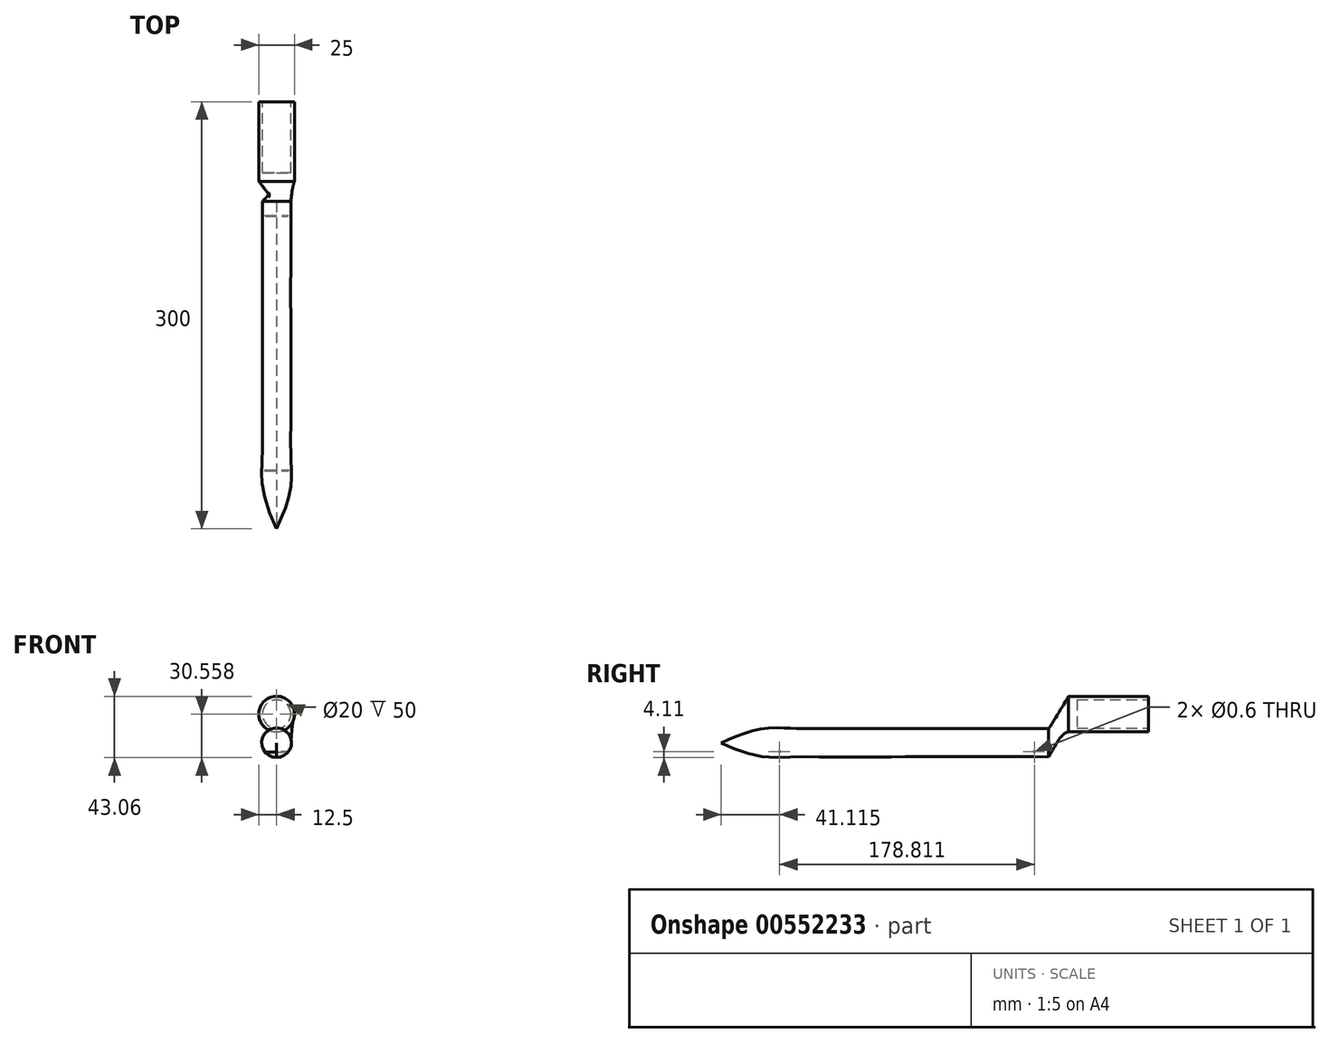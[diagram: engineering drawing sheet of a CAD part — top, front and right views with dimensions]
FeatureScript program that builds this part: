
annotation { "Feature Type Name" : "Feature", "Feature Type Description" : "" }
export const myFeature = defineFeature(function(context is Context, id is Id, definition is map)
    precondition{}
    {
        {
            var Q0;
            Q0=qCreatedBy(makeId("Right.planeOp"),FACE);
            var sketch = newSketch(context, id + "F0", { "sketchPlane" : qUnion([Q0])});
            skLineSegment(sketch, "E0.top", {"start": v(-74.77, -35) * mm, "end": v(75.63, -35) * mm});
            skLineSegment(sketch, "E0.right", {"start": v(150, 15.16) * mm, "end": v(150, -6.84) * mm});
            skPoint(sketch, "E1.orphan", {"position": v(-150, -15) * mm});
            skPoint(sketch, "E2.orphan", {"position": v(-150, -35) * mm});
            skPoint(sketch, "E3.orphan", {"position": v(150, 35) * mm});
            skLineSegment(sketch, "E4", {"start": v(150, 35) * mm, "end": v(80, 23.33) * mm});
            skLineSegment(sketch, "E5", {"start": v(-150, -35) * mm, "end": v(-150, -15) * mm});
            skLineSegment(sketch, "E6", {"start": v(-150, -35) * mm, "end": v(-74.77, -35) * mm});
            skLineSegment(sketch, "E7", {"start": v(150, 35) * mm, "end": v(150, -35) * mm});
            skLineSegment(sketch, "E8", {"start": v(75.63, -35) * mm, "end": v(150, -35) * mm});
            skPoint(sketch, "E9.0.internal.orphan", {"position": v(-150, -25) * mm});
            skLineSegment(sketch, "E10", {"start": v(-150, -15) * mm, "end": v(80, -15) * mm});
            skLineSegment(sketch, "E11", {"start": v(80, -15) * mm, "end": v(80, 23.33) * mm});
            skSolve(sketch);
        }
        {
            var Q0;
            Q0=makeQuery(id+"F0.imprint","IMPRINT",FACE,{"disambiguationData":[TD([[makeQuery(id+"F0.imprint","IMPRINT",EDGE,{"derivedFrom":sQuery(id+"F0.wireOp",EDGE,"E0.bottom")}),-1.0]])]});
            var Q1;
            Q1=makeQuery(id+"F0.imprint","IMPRINT",FACE,{"disambiguationData":[TD([[makeQuery(id+"F0.imprint","IMPRINT",EDGE,{"derivedFrom":sQuery(id+"F0.wireOp",EDGE,"E0.top")}),1.0]])]});
            extrude(context, id + "F1", {"entities" : qUnion([Q0, Q1]), "endBound" : BoundingType.SYMMETRIC, "depth" : 42 * mm, "offsetDistance" : 25 * mm});
        }
        {
            var Q0;
            Q0=makeQuery(id+"F1.opExtrude","SWEPT_FACE",FACE,{"disambiguationData":[OSD([sQuery(id+"F0.wireOp",EDGE,"E7")])]});
            var sketch = newSketch(context, id + "F2", { "sketchPlane" : qUnion([Q0])});
            skPoint(sketch, "E12.start.orphan", {"position": v(0, 35) * mm});
            skCircle(sketch, "E13", {"center": v(0, -4.85) * mm, "radius": 10 * mm});
            skPoint(sketch, "E14.orphan", {"position": v(0, -35) * mm});
            skSolve(sketch);
        }
        {
            var Q0;
            Q0=makeQuery(id+"F2.imprint","IMPRINT",FACE,{"disambiguationData":[TD([[makeQuery(id+"F2.imprint","IMPRINT",EDGE,{"derivedFrom":sQuery(id+"F2.wireOp",EDGE,"E13")}),1.0]])]});
            extrude(context, id + "F3", {"entities" : qUnion([Q0]), "operationType" : NewBodyOperationType.REMOVE, "oppositeDirection" : true, "depth" : 50 * mm, "offsetDistance" : 25 * mm});
        }
        {
            var Q0;
            Q0=makeQuery(id+"F1.opExtrude","SWEPT_FACE",FACE,{"disambiguationData":[OSD([sQuery(id+"F0.wireOp",EDGE,"E5")])]});
            var sketch = newSketch(context, id + "F4", { "sketchPlane" : qUnion([Q0])});
            skLineSegment(sketch, "E15.bottom", {"start": v(-10, -15) * mm, "end": v(10, -15) * mm});
            skLineSegment(sketch, "E15.top", {"start": v(-10, -35) * mm, "end": v(10, -35) * mm});
            skLineSegment(sketch, "E15.left", {"start": v(-10, -15) * mm, "end": v(-10, -35) * mm});
            skLineSegment(sketch, "E15.right", {"start": v(10, -15) * mm, "end": v(10, -35) * mm});
            skPoint(sketch, "E15.middle", {"position": v(0, -25) * mm});
            skPoint(sketch, "E15.middle.positionSnap0", {"position": v(21, -25) * mm});
            skPoint(sketch, "E15.middle.positionSnap1", {"position": v(0, -35) * mm});
            skPoint(sketch, "E15.centerSnap0", {"position": v(21, -25) * mm});
            skPoint(sketch, "E15.centerSnap1", {"position": v(0, -35) * mm});
            skSolve(sketch);
        }
        {
            var Q0;
            Q0=makeQuery(id+"F4.imprint","IMPRINT",FACE,{"disambiguationData":[TD([[makeQuery(id+"F4.imprint","IMPRINT",EDGE,{"derivedFrom":sQuery(id+"F4.wireOp",EDGE,"E15.bottom")}),1.0]])]});
            extrude(context, id + "F5", {"entities" : qUnion([Q0]), "operationType" : NewBodyOperationType.REMOVE, "oppositeDirection" : true, "depth" : 230 * mm, "offsetDistance" : 25 * mm});
        }
        {
            var Q0;
            Q0=qCreatedBy(makeId("Front.planeOp"),FACE);
            cPlane(context, id + "F6", {"entities" : qUnion([Q0]), "cplaneType" : CPlaneType.OFFSET, "offset" : 150 * mm, "width" : 150 * mm, "height" : 150 * mm});
        }
        {
            var Q0;
            Q0=qCreatedBy(id+"F6.planeOp",FACE);
            var sketch = newSketch(context, id + "F7", { "sketchPlane" : qUnion([Q0])});
            skPoint(sketch, "E16", {"position": v(0, -25.1) * mm});
            skSolve(sketch);
        }
        {
            var Q0;
            Q0=qCreatedBy(id+"F6.planeOp",FACE);
            cPlane(context, id + "F8", {"entities" : qUnion([Q0]), "cplaneType" : CPlaneType.OFFSET, "offset" : 30 * mm, "oppositeDirection" : true, "width" : 150 * mm, "height" : 150 * mm});
        }
        {
            var Q0;
            Q0=qCreatedBy(id+"F8.planeOp",FACE);
            var sketch = newSketch(context, id + "F9", { "sketchPlane" : qUnion([Q0])});
            skCircle(sketch, "E17", {"center": v(0, -25.02) * mm, "radius": 10 * mm});
            skSolve(sketch);
        }
        {
            var Q0;
            Q0=qCreatedBy(id+"F6.planeOp",FACE);
            cPlane(context, id + "F10", {"entities" : qUnion([Q0]), "cplaneType" : CPlaneType.OFFSET, "offset" : 230 * mm, "oppositeDirection" : true, "width" : 150 * mm, "height" : 150 * mm});
        }
        {
            var Q0;
            Q0=qCreatedBy(id+"F10.planeOp",FACE);
            var sketch = newSketch(context, id + "F11", { "sketchPlane" : qUnion([Q0])});
            skCircle(sketch, "E18", {"center": v(0, -24.92) * mm, "radius": 10 * mm});
            skSolve(sketch);
        }
        {
            var Q0;
            Q0=qCreatedBy(id+"F6.planeOp",FACE);
            cPlane(context, id + "F12", {"entities" : qUnion([Q0]), "cplaneType" : CPlaneType.OFFSET, "offset" : 115 * mm, "oppositeDirection" : true, "width" : 150 * mm, "height" : 150 * mm});
        }
        {
            var Q0;
            Q0=qCreatedBy(id+"F12.planeOp",FACE);
            var sketch = newSketch(context, id + "F13", { "sketchPlane" : qUnion([Q0])});
            skCircle(sketch, "E19", {"center": v(0, -24.97) * mm, "radius": 10 * mm});
            skSolve(sketch);
        }
        {
            var Q0;
            {var subQ4=sQuery(id+"F0.wireOp",EDGE,"E5");Q0=makeQuery(id+"F5.boolean.opBoolean","SPLIT",FACE,{"disambiguationData":[TD([makeQuery(id+"F5.opExtrude","SWEPT_FACE",FACE,{"disambiguationData":[OSD([sQuery(id+"F4.wireOp",EDGE,"E15.right")])]})])],"derivedFrom":makeQuery(id+"F1.opExtrude","SWEPT_FACE",FACE,{"disambiguationData":[OSD([subQ4])]})});}
            var Q1;
            {var subQ4=sQuery(id+"F0.wireOp",EDGE,"E5");Q1=makeQuery(id+"F5.boolean.opBoolean","SPLIT",FACE,{"disambiguationData":[TD([makeQuery(id+"F5.opExtrude","SWEPT_FACE",FACE,{"disambiguationData":[OSD([sQuery(id+"F4.wireOp",EDGE,"E15.left")])]})])],"derivedFrom":makeQuery(id+"F1.opExtrude","SWEPT_FACE",FACE,{"disambiguationData":[OSD([subQ4])]})});}
            extrude(context, id + "F14", {"entities" : qUnion([Q0, Q1]), "operationType" : NewBodyOperationType.REMOVE, "oppositeDirection" : true, "depth" : 230 * mm, "offsetDistance" : 25 * mm});
        }
        {
            var Q0;
            Q0=qCreatedBy(id+"F8.planeOp",FACE);
            cPlane(context, id + "F15", {"entities" : qUnion([Q0]), "cplaneType" : CPlaneType.OFFSET, "offset" : 45 * mm, "oppositeDirection" : true, "width" : 150 * mm, "height" : 150 * mm});
        }
        {
            var Q0;
            Q0=qCreatedBy(id+"F15.planeOp",FACE);
            var sketch = newSketch(context, id + "F16", { "sketchPlane" : qUnion([Q0])});
            skCircle(sketch, "E20", {"center": v(0, -25.05) * mm, "radius": 10 * mm});
            skSolve(sketch);
        }
        {
            var Q0;
            Q0=qCreatedBy(id+"F15.planeOp",FACE);
            cPlane(context, id + "F17", {"entities" : qUnion([Q0]), "cplaneType" : CPlaneType.OFFSET, "offset" : 23 * mm, "width" : 150 * mm, "height" : 150 * mm});
        }
        {
            var Q0;
            Q0=qCreatedBy(id+"F17.planeOp",FACE);
            var sketch = newSketch(context, id + "F18", { "sketchPlane" : qUnion([Q0])});
            skCircle(sketch, "E21", {"center": v(0, -24.89) * mm, "radius": 10 * mm});
            skSolve(sketch);
        }
        {
            var Q1;
            Q1=makeQuery(id+"F11.imprint","IMPRINT",FACE,{"disambiguationData":[TD([[makeQuery(id+"F11.imprint","IMPRINT",EDGE,{"derivedFrom":sQuery(id+"F11.wireOp",EDGE,"E18")}),1.0]])]});
            var Q2;
            Q2=makeQuery(id+"F13.imprint","IMPRINT",FACE,{"disambiguationData":[TD([[makeQuery(id+"F13.imprint","IMPRINT",EDGE,{"derivedFrom":sQuery(id+"F13.wireOp",EDGE,"E19")}),1.0]])]});
            var Q3;
            Q3=makeQuery(id+"F16.imprint","IMPRINT",FACE,{"disambiguationData":[TD([[makeQuery(id+"F16.imprint","IMPRINT",EDGE,{"derivedFrom":sQuery(id+"F16.wireOp",EDGE,"E20")}),1.0]])]});
            var Q4;
            Q4=makeQuery(id+"F18.imprint","IMPRINT",FACE,{"disambiguationData":[TD([[makeQuery(id+"F18.imprint","IMPRINT",EDGE,{"derivedFrom":sQuery(id+"F18.wireOp",EDGE,"E21")}),1.0]])]});
            var Q5;
            Q5=makeQuery(id+"F9.imprint","IMPRINT",FACE,{"disambiguationData":[TD([[makeQuery(id+"F9.imprint","IMPRINT",EDGE,{"derivedFrom":sQuery(id+"F9.wireOp",EDGE,"E17")}),1.0]])]});
            var Q6;
            Q6=sQuery(id+"F7.wireOp",VERTEX,"E16");
            loft(context, id + "F19", {"operationType" : NewBodyOperationType.ADD, "sheetProfilesArray" : [{ "sheetProfileEntities" : qUnion([Q1]) }, { "sheetProfileEntities" : qUnion([Q2]) }, { "sheetProfileEntities" : qUnion([Q3]) }, { "sheetProfileEntities" : qUnion([Q4]) }, { "sheetProfileEntities" : qUnion([Q5]) }, { "sheetProfileEntities" : qUnion([Q6]) }]});
        }
        {
            var Q0;
            Q0=makeQuery(id+"F1.opExtrude","SWEPT_FACE",FACE,{"disambiguationData":[OSD([sQuery(id+"F0.wireOp",EDGE,"E7")])]});
            var sketch = newSketch(context, id + "F20", { "sketchPlane" : qUnion([Q0])});
            skCircle(sketch, "E22", {"center": v(0, -4.85) * mm, "radius": 12.5 * mm});
            skSolve(sketch);
        }
        {
            var Q0;
            Q0=makeQuery(id+"F20.imprint","IMPRINT",FACE,{"disambiguationData":[TD([[makeQuery(id+"F20.imprint","IMPRINT",EDGE,{"derivedFrom":sQuery(id+"F20.wireOp",EDGE,"E22")}),-1.0]])]});
            extrude(context, id + "F21", {"entities" : qUnion([Q0]), "operationType" : NewBodyOperationType.REMOVE, "oppositeDirection" : true, "depth" : 70 * mm, "offsetDistance" : 25 * mm});
        }
        {
            var Q0;
            {var subQ0=sQuery(id+"F0.wireOp",EDGE,"E11");var subQ5=sQuery(id+"F0.wireOp",EDGE,"E5");var subQ10=sQuery(id+"F4.wireOp",EDGE,"E15.right");var subQ11=makeQuery(id+"F1.opExtrude","SWEPT_FACE",FACE,{"disambiguationData":[OSD([subQ5])]});var subQ12=sQuery(id+"F4.wireOp",EDGE,"E15.left");Q0=makeQuery(id+"F14.boolean.opBoolean","MERGE",FACE,{"derivedFrom":[makeQuery(id+"F5.boolean.opBoolean","MERGE",FACE,{"derivedFrom":[makeQuery(id+"F1.opExtrude","SWEPT_FACE",FACE,{"disambiguationData":[OSD([subQ0])]}),makeQuery(id+"F5.opExtrude","CAP_FACE",FACE,{"disambiguationData":[OSD([sQuery(id+"F4.wireOp",EDGE,"E15.bottom"),sQuery(id+"F4.wireOp",EDGE,"E15.top"),subQ12,subQ10])],"isStart":false})]}),makeQuery(id+"F14.opExtrude","CAP_FACE",FACE,{"disambiguationData":[OSD([subQ5]),TDD([makeQuery(id+"F5.boolean.opBoolean","SPLIT",FACE,{"disambiguationData":[TD([makeQuery(id+"F5.opExtrude","SWEPT_FACE",FACE,{"disambiguationData":[OSD([subQ12])]})])],"derivedFrom":subQ11})])],"isStart":false}),makeQuery(id+"F14.opExtrude","CAP_FACE",FACE,{"disambiguationData":[OSD([subQ5]),TDD([makeQuery(id+"F5.boolean.opBoolean","SPLIT",FACE,{"disambiguationData":[TD([makeQuery(id+"F5.opExtrude","SWEPT_FACE",FACE,{"disambiguationData":[OSD([subQ10])]})])],"derivedFrom":subQ11})])],"isStart":false})]});}
            extrude(context, id + "F22", {"entities" : qUnion([Q0]), "operationType" : NewBodyOperationType.REMOVE, "oppositeDirection" : true, "depth" : 14 * mm, "offsetDistance" : 25 * mm});
        }
        {
            var Q0;
            Q0=qCreatedBy(id+"F10.planeOp",FACE);
            var sketch = newSketch(context, id + "F23", { "sketchPlane" : qUnion([Q0])});
            skCircle(sketch, "E23", {"center": v(0, -14.65) * mm, "radius": 55.86 * mm});
            skSolve(sketch);
        }
        {
            var Q0;
            Q0=makeQuery(id+"F23.imprint","IMPRINT",FACE,{"disambiguationData":[TD([[makeQuery(id+"F23.imprint","IMPRINT",EDGE,{"derivedFrom":sQuery(id+"F23.wireOp",EDGE,"E23")}),1.0]])]});
            extrude(context, id + "F24", {"entities" : qUnion([Q0]), "operationType" : NewBodyOperationType.REMOVE, "oppositeDirection" : true, "depth" : 14 * mm, "offsetDistance" : 25 * mm});
        }
        {
            var Q0;
            Q0=makeQuery(id+"F24.boolean.opBoolean","MERGE",FACE,{"derivedFrom":[makeQuery(id+"F22.boolean.opBoolean","COPY",FACE,{"derivedFrom":makeQuery(id+"F22.opExtrude","CAP_FACE",FACE,{"disambiguationData":[OSD([sQuery(id+"F0.wireOp",EDGE,"E5"),sQuery(id+"F0.wireOp",EDGE,"E11"),sQuery(id+"F4.wireOp",EDGE,"E15.bottom"),sQuery(id+"F4.wireOp",EDGE,"E15.top"),sQuery(id+"F4.wireOp",EDGE,"E15.left"),sQuery(id+"F4.wireOp",EDGE,"E15.right")])],"isStart":false})}),makeQuery(id+"F24.opExtrude","CAP_FACE",FACE,{"disambiguationData":[OSD([sQuery(id+"F23.wireOp",EDGE,"E23")])],"isStart":false})]});
            var Q1;
            Q1=makeQuery(id+"F24.boolean.opBoolean","MERGE",FACE,{"derivedFrom":[makeQuery(id+"F21.boolean.opBoolean","COPY",FACE,{"derivedFrom":makeQuery(id+"F21.opExtrude","CAP_FACE",FACE,{"disambiguationData":[OSD([sQuery(id+"F0.wireOp",EDGE,"E4"),sQuery(id+"F0.wireOp",EDGE,"E7"),sQuery(id+"F0.wireOp",EDGE,"E8"),sQuery(id+"F20.wireOp",EDGE,"E22")])],"isStart":false})}),makeQuery(id+"F24.opExtrude","CAP_FACE",FACE,{"disambiguationData":[OSD([sQuery(id+"F23.wireOp",EDGE,"E23")])],"isStart":true})]});
            loft(context, id + "F25", {"sheetProfilesArray" : [{ "sheetProfileEntities" : qUnion([Q0]) }, { "sheetProfileEntities" : qUnion([Q1]) }]});
        }
        {
            var Q0;
            Q0=qCreatedBy(makeId("Right.planeOp"),FACE);
            cPlane(context, id + "F26", {"entities" : qUnion([Q0]), "cplaneType" : CPlaneType.OFFSET, "offset" : 25 * mm, "width" : 150 * mm, "height" : 150 * mm});
        }
        {
            var Q0;
            Q0=qCreatedBy(id+"F26.planeOp",FACE);
            var sketch = newSketch(context, id + "F27", { "sketchPlane" : qUnion([Q0])});
            skCircle(sketch, "E24", {"center": v(-108.88, -31.3) * mm, "radius": 0.3 * mm});
            skCircle(sketch, "E25", {"center": v(69.93, -31.3) * mm, "radius": 0.3 * mm});
            skSolve(sketch);
        }
        {
            var Q0;
            Q0=makeQuery(id+"F27.imprint","IMPRINT",FACE,{"disambiguationData":[TD([[makeQuery(id+"F27.imprint","IMPRINT",EDGE,{"derivedFrom":sQuery(id+"F27.wireOp",EDGE,"E24")}),1.0]])]});
            var Q1;
            Q1=makeQuery(id+"F27.imprint","IMPRINT",FACE,{"disambiguationData":[TD([[makeQuery(id+"F27.imprint","IMPRINT",EDGE,{"derivedFrom":sQuery(id+"F27.wireOp",EDGE,"E25")}),1.0]])]});
            extrude(context, id + "F28", {"entities" : qUnion([Q0, Q1]), "operationType" : NewBodyOperationType.REMOVE, "oppositeDirection" : true, "depth" : 50 * mm, "offsetDistance" : 25 * mm});
        }
    });
